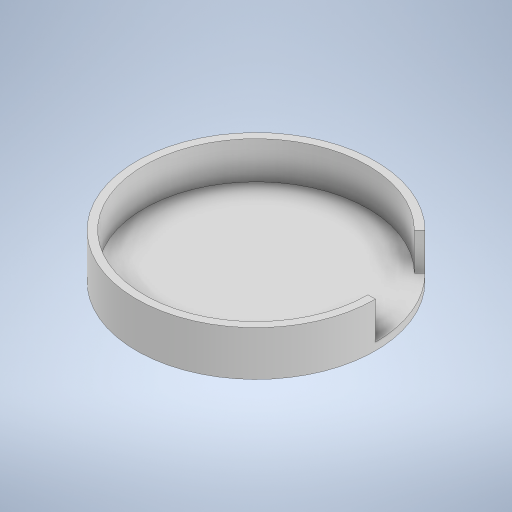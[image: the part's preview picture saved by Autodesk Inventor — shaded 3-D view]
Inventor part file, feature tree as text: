
AUTODESK INVENTOR PART (.ipt)
format: ipt  version: 2024 (Build 280153000, 153)  size: 251,904 bytes
history: native  units: in
note: dims shown in document units (in); Inventor stores cm internally (conversion verified against a paired STEP export)
features: extrude x3, sketch x3
ambient origin geometry x8: Origin, YZ Plane, XZ Plane, XY Plane, X Axis, Y Axis, Z Axis, Center Point
bodies: Body1 (feature_tree)
feature tree (6):
  extrude  "Extrusion3"  Depth=3.7795in
  extrude  "Extrusion4"  Depth=0.7087in
  extrude  "Extrusion5"  Depth=1.8898in
  sketch  "Sketch1"  dims[d0=3.5433in d1=3.7795in]
  sketch  "Sketch3"  dims[d7=0.7087in d8=0.0in d9=3.5433in]
  sketch  "Sketch4"  dims[d10=0.1181in d11=0.0in d12=1.8898in d13=0.0in d14=1.8898in d15=45.0deg d16=1.8898in d17=0.7874in d18=0.0in]
